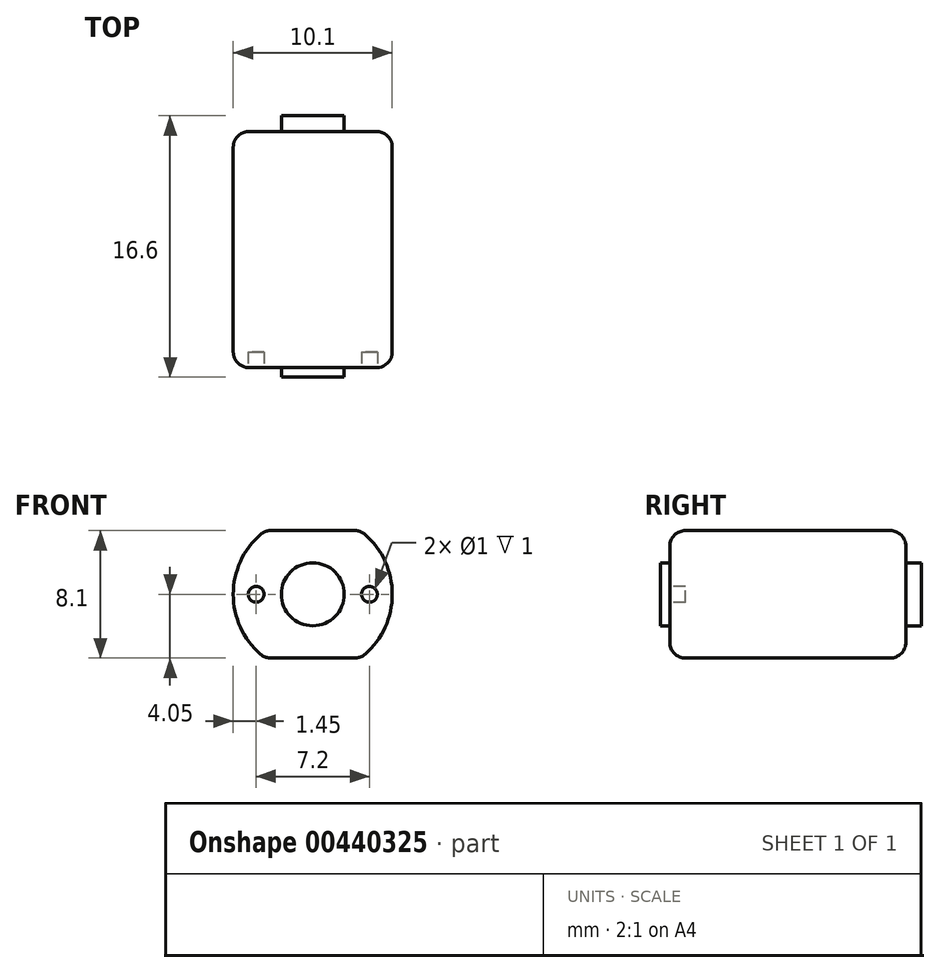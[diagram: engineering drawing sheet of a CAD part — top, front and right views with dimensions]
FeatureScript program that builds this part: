
annotation { "Feature Type Name" : "Feature", "Feature Type Description" : "" }
export const myFeature = defineFeature(function(context is Context, id is Id, definition is map)
    precondition{}
    {
        {
            var Q0;
            Q0=qCreatedBy(makeId("Front.planeOp"),FACE);
            var sketch = newSketch(context, id + "F0", { "sketchPlane" : qUnion([Q0])});
            skArc(sketch, "E0", {"start": v(-3.02, 4.05) * mm, "mid": v(-5.05, 0) * mm, "end": v(-3.02, -4.05) * mm});
            skLineSegment(sketch, "E1.bottom", {"start": v(-3.02, 4.05) * mm, "end": v(3.02, 4.05) * mm});
            skLineSegment(sketch, "E1.top", {"start": v(-3.02, -4.05) * mm, "end": v(3.02, -4.05) * mm});
            skLineSegment(sketch, "E1.left", {"start": v(-3.02, 4.05) * mm, "end": v(-3.02, -4.05) * mm});
            skLineSegment(sketch, "E1.right", {"start": v(3.02, 4.05) * mm, "end": v(3.02, -4.05) * mm});
            skArc(sketch, "E2.trimOffspring", {"start": v(3.02, -4.05) * mm, "mid": v(5.05, 0) * mm, "end": v(3.02, 4.05) * mm});
            skSolve(sketch);
        }
        {
            var Q0;
            Q0=makeQuery(id+"F0.imprint","IMPRINT",FACE,{"disambiguationData":[TD([[makeQuery(id+"F0.imprint","IMPRINT",EDGE,{"derivedFrom":sQuery(id+"F0.wireOp",EDGE,"E1.bottom")}),-1.0]])]});
            var Q1;
            Q1=makeQuery(id+"F0.imprint","IMPRINT",FACE,{"disambiguationData":[TD([[makeQuery(id+"F0.imprint","IMPRINT",EDGE,{"derivedFrom":sQuery(id+"F0.wireOp",EDGE,"E1.right")}),1.0]])]});
            var Q2;
            Q2=makeQuery(id+"F0.imprint","IMPRINT",FACE,{"disambiguationData":[TD([[makeQuery(id+"F0.imprint","IMPRINT",EDGE,{"derivedFrom":sQuery(id+"F0.wireOp",EDGE,"E0")}),1.0]])]});
            extrude(context, id + "F1", {"entities" : qUnion([Q0, Q1, Q2]), "endBound" : BoundingType.SYMMETRIC, "depth" : 15 * mm});
        }
        {
            var Q0;
            Q0=makeQuery(id+"F1.opExtrude","CAP_FACE",FACE,{"disambiguationData":[OSD([sQuery(id+"F0.wireOp",EDGE,"E0"),sQuery(id+"F0.wireOp",EDGE,"E1.bottom"),sQuery(id+"F0.wireOp",EDGE,"E1.top"),sQuery(id+"F0.wireOp",EDGE,"E2.trimOffspring")])],"isStart":false});
            var sketch = newSketch(context, id + "F2", { "sketchPlane" : qUnion([Q0])});
            skCircle(sketch, "E3", {"center": v(0, 0) * mm, "radius": 2 * mm});
            skSolve(sketch);
        }
        {
            var Q0;
            Q0=makeQuery(id+"F2.imprint","IMPRINT",FACE,{"disambiguationData":[TD([[makeQuery(id+"F2.imprint","IMPRINT",EDGE,{"derivedFrom":sQuery(id+"F2.wireOp",EDGE,"E3")}),1.0]])]});
            extrude(context, id + "F3", {"entities" : qUnion([Q0]), "operationType" : NewBodyOperationType.ADD, "depth" : 0.6 * mm});
        }
        {
            var Q0;
            Q0=makeQuery(id+"F1.opExtrude","CAP_FACE",FACE,{"disambiguationData":[OSD([sQuery(id+"F0.wireOp",EDGE,"E0"),sQuery(id+"F0.wireOp",EDGE,"E1.bottom"),sQuery(id+"F0.wireOp",EDGE,"E1.top"),sQuery(id+"F0.wireOp",EDGE,"E2.trimOffspring")])],"isStart":true});
            var sketch = newSketch(context, id + "F4", { "sketchPlane" : qUnion([Q0])});
            skCircle(sketch, "E4", {"center": v(0, 0) * mm, "radius": 2 * mm});
            skSolve(sketch);
        }
        {
            var Q0;
            Q0=makeQuery(id+"F4.imprint","IMPRINT",FACE,{"disambiguationData":[TD([[makeQuery(id+"F4.imprint","IMPRINT",EDGE,{"derivedFrom":sQuery(id+"F4.wireOp",EDGE,"E4")}),1.0]])]});
            extrude(context, id + "F5", {"entities" : qUnion([Q0]), "operationType" : NewBodyOperationType.ADD, "depth" : 1 * mm});
        }
        {
            var Q0;
            Q0=makeQuery(id+"F1.opExtrude","CAP_FACE",FACE,{"disambiguationData":[OSD([sQuery(id+"F0.wireOp",EDGE,"E0"),sQuery(id+"F0.wireOp",EDGE,"E1.bottom"),sQuery(id+"F0.wireOp",EDGE,"E1.top"),sQuery(id+"F0.wireOp",EDGE,"E2.trimOffspring")])],"isStart":false});
            var sketch = newSketch(context, id + "F6", { "sketchPlane" : qUnion([Q0])});
            skLineSegment(sketch, "E5", {"start": v(5.05, 0) * mm, "end": v(4.1, 0) * mm});
            skCircle(sketch, "E6", {"center": v(-3.6, 0) * mm, "radius": 0.5 * mm});
            skCircle(sketch, "E7", {"center": v(3.6, 0) * mm, "radius": 0.5 * mm});
            skLineSegment(sketch, "E8.trimOffspring", {"start": v(-4.1, 0) * mm, "end": v(-5.05, 0) * mm});
            skSolve(sketch);
        }
        {
            var Q0;
            Q0 = qSketchRegion(id + "F6", true);
            extrude(context, id + "F7", {"entities" : qUnion([Q0]), "operationType" : NewBodyOperationType.REMOVE, "oppositeDirection" : true, "depth" : 1 * mm});
        }
        {
            var Q0;
            Q0=makeQuery(id+"F1.opExtrude","SWEPT_EDGE",EDGE,{"disambiguationData":[OSD([sQuery(id+"F0.wireOp",EDGE,"E1.top"),sQuery(id+"F0.wireOp",EDGE,"E1.right"),sQuery(id+"F0.wireOp",EDGE,"E2.trimOffspring")])]});
            var Q1;
            Q1=makeQuery(id+"F1.opExtrude","SWEPT_EDGE",EDGE,{"disambiguationData":[OSD([sQuery(id+"F0.wireOp",EDGE,"E0"),sQuery(id+"F0.wireOp",EDGE,"E1.top"),sQuery(id+"F0.wireOp",EDGE,"E1.left")])]});
            var Q2;
            Q2=makeQuery(id+"F1.opExtrude","SWEPT_EDGE",EDGE,{"disambiguationData":[OSD([sQuery(id+"F0.wireOp",EDGE,"E1.bottom"),sQuery(id+"F0.wireOp",EDGE,"E1.right"),sQuery(id+"F0.wireOp",EDGE,"E2.trimOffspring")])]});
            var Q3;
            Q3=makeQuery(id+"F1.opExtrude","SWEPT_EDGE",EDGE,{"disambiguationData":[OSD([sQuery(id+"F0.wireOp",EDGE,"E0"),sQuery(id+"F0.wireOp",EDGE,"E1.bottom"),sQuery(id+"F0.wireOp",EDGE,"E1.left")])]});
            var Q4;
            Q4=makeQuery(id+"F1.opExtrude","CAP_EDGE",EDGE,{"disambiguationData":[OSD([sQuery(id+"F0.wireOp",EDGE,"E1.bottom")])],"isStart":false});
            var Q5;
            Q5=makeQuery(id+"F1.opExtrude","CAP_EDGE",EDGE,{"disambiguationData":[OSD([sQuery(id+"F0.wireOp",EDGE,"E0")])],"isStart":false});
            var Q6;
            Q6=makeQuery(id+"F1.opExtrude","CAP_EDGE",EDGE,{"disambiguationData":[OSD([sQuery(id+"F0.wireOp",EDGE,"E2.trimOffspring")])],"isStart":false});
            var Q7;
            Q7=makeQuery(id+"F1.opExtrude","CAP_EDGE",EDGE,{"disambiguationData":[OSD([sQuery(id+"F0.wireOp",EDGE,"E1.top")])],"isStart":false});
            var Q8;
            Q8=makeQuery(id+"F1.opExtrude","CAP_EDGE",EDGE,{"disambiguationData":[OSD([sQuery(id+"F0.wireOp",EDGE,"E0")])],"isStart":true});
            var Q9;
            Q9=makeQuery(id+"F1.opExtrude","CAP_EDGE",EDGE,{"disambiguationData":[OSD([sQuery(id+"F0.wireOp",EDGE,"E1.bottom")])],"isStart":true});
            var Q10;
            Q10=makeQuery(id+"F1.opExtrude","CAP_EDGE",EDGE,{"disambiguationData":[OSD([sQuery(id+"F0.wireOp",EDGE,"E2.trimOffspring")])],"isStart":true});
            var Q11;
            Q11=makeQuery(id+"F1.opExtrude","CAP_EDGE",EDGE,{"disambiguationData":[OSD([sQuery(id+"F0.wireOp",EDGE,"E1.top")])],"isStart":true});
            fillet(context, id + "F8", {"entities" : qUnion([Q0, Q1, Q2, Q3, Q4, Q5, Q6, Q7, Q8, Q9, Q10, Q11]), "radius" : 1 * mm, "tangentPropagation" : true, "allowEdgeOverflow" : false});
        }
    });
